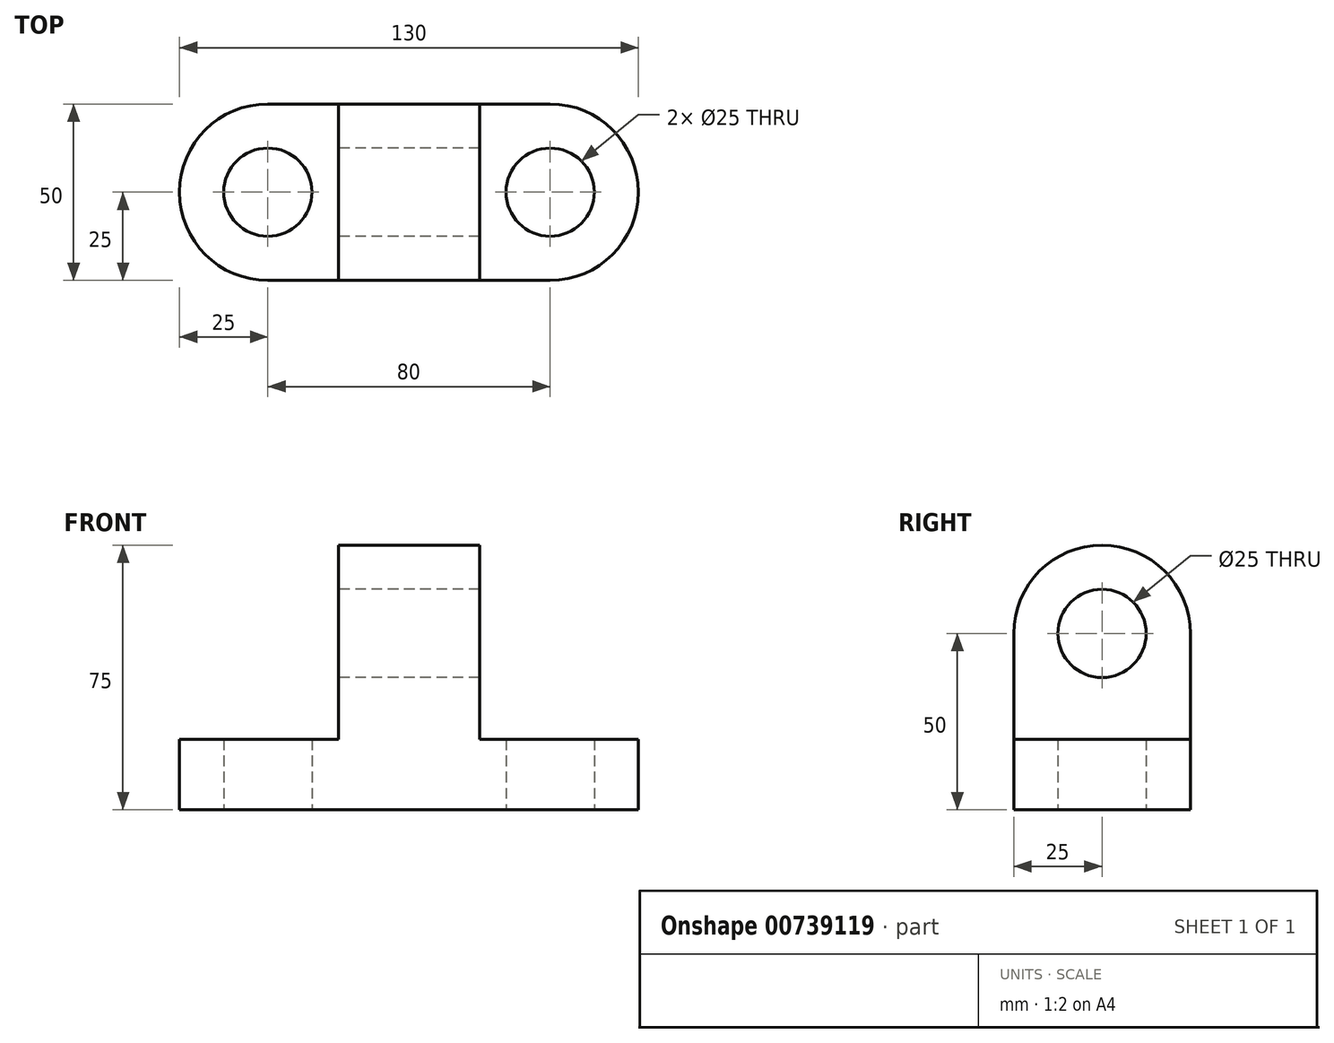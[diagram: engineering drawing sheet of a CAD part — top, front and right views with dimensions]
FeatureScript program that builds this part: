
annotation { "Feature Type Name" : "Feature", "Feature Type Description" : "" }
export const myFeature = defineFeature(function(context is Context, id is Id, definition is map)
    precondition{}
    {
        {
            var Q0;
            Q0=qCreatedBy(makeId("Right.planeOp"),FACE);
            var sketch = newSketch(context, id + "F0", { "sketchPlane" : qUnion([Q0])});
            skLineSegment(sketch, "E0", {"start": v(-25, 0) * mm, "end": v(25, 0) * mm});
            skLineSegment(sketch, "E1", {"start": v(25, 0) * mm, "end": v(25, 50) * mm});
            skLineSegment(sketch, "E2", {"start": v(25, 50) * mm, "end": v(-25, 50) * mm});
            skLineSegment(sketch, "E3", {"start": v(-25, 50) * mm, "end": v(-25, 0) * mm});
            skArc(sketch, "E4", {"start": v(25, 50) * mm, "mid": v(0, 75) * mm, "end": v(-25, 50) * mm});
            skCircle(sketch, "E5", {"center": v(0, 50) * mm, "radius": 12.5 * mm});
            skSolve(sketch);
        }
        {
            var Q0;
            Q0 = qSketchRegion(id + "F0", true);
            extrude(context, id + "F1", {"entities" : qUnion([Q0]), "endBound" : BoundingType.SYMMETRIC, "depth" : 40 * mm, "offsetDistance" : 25 * mm});
        }
        {
            var Q0;
            Q0=qCreatedBy(makeId("Top.planeOp"),FACE);
            var sketch = newSketch(context, id + "F2", { "sketchPlane" : qUnion([Q0])});
            skLineSegment(sketch, "E6", {"start": v(0, 25) * mm, "end": v(0, -25) * mm});
            skLineSegment(sketch, "E7", {"start": v(-40, 25) * mm, "end": v(-40, -25) * mm});
            skLineSegment(sketch, "E8", {"start": v(-40, 25) * mm, "end": v(40, 25) * mm});
            skLineSegment(sketch, "E9", {"start": v(40, -25) * mm, "end": v(-40, -25) * mm});
            skLineSegment(sketch, "E10", {"start": v(40, 25) * mm, "end": v(40, 0) * mm});
            skLineSegment(sketch, "E11", {"start": v(40, 0) * mm, "end": v(40, -25) * mm});
            skArc(sketch, "E12", {"start": v(-40, 25) * mm, "mid": v(-65, 0) * mm, "end": v(-40, -25) * mm});
            skArc(sketch, "E13", {"start": v(40, -25) * mm, "mid": v(65, 0) * mm, "end": v(40, 25) * mm});
            skCircle(sketch, "E14", {"center": v(-40, 0) * mm, "radius": 12.5 * mm});
            skCircle(sketch, "E15", {"center": v(40, 0) * mm, "radius": 12.5 * mm});
            skSolve(sketch);
        }
        {
            var Q0;
            Q0 = qSketchRegion(id + "F2", true);
            extrude(context, id + "F3", {"entities" : qUnion([Q0]), "operationType" : NewBodyOperationType.ADD, "depth" : 20 * mm, "offsetDistance" : 25 * mm});
        }
    });
